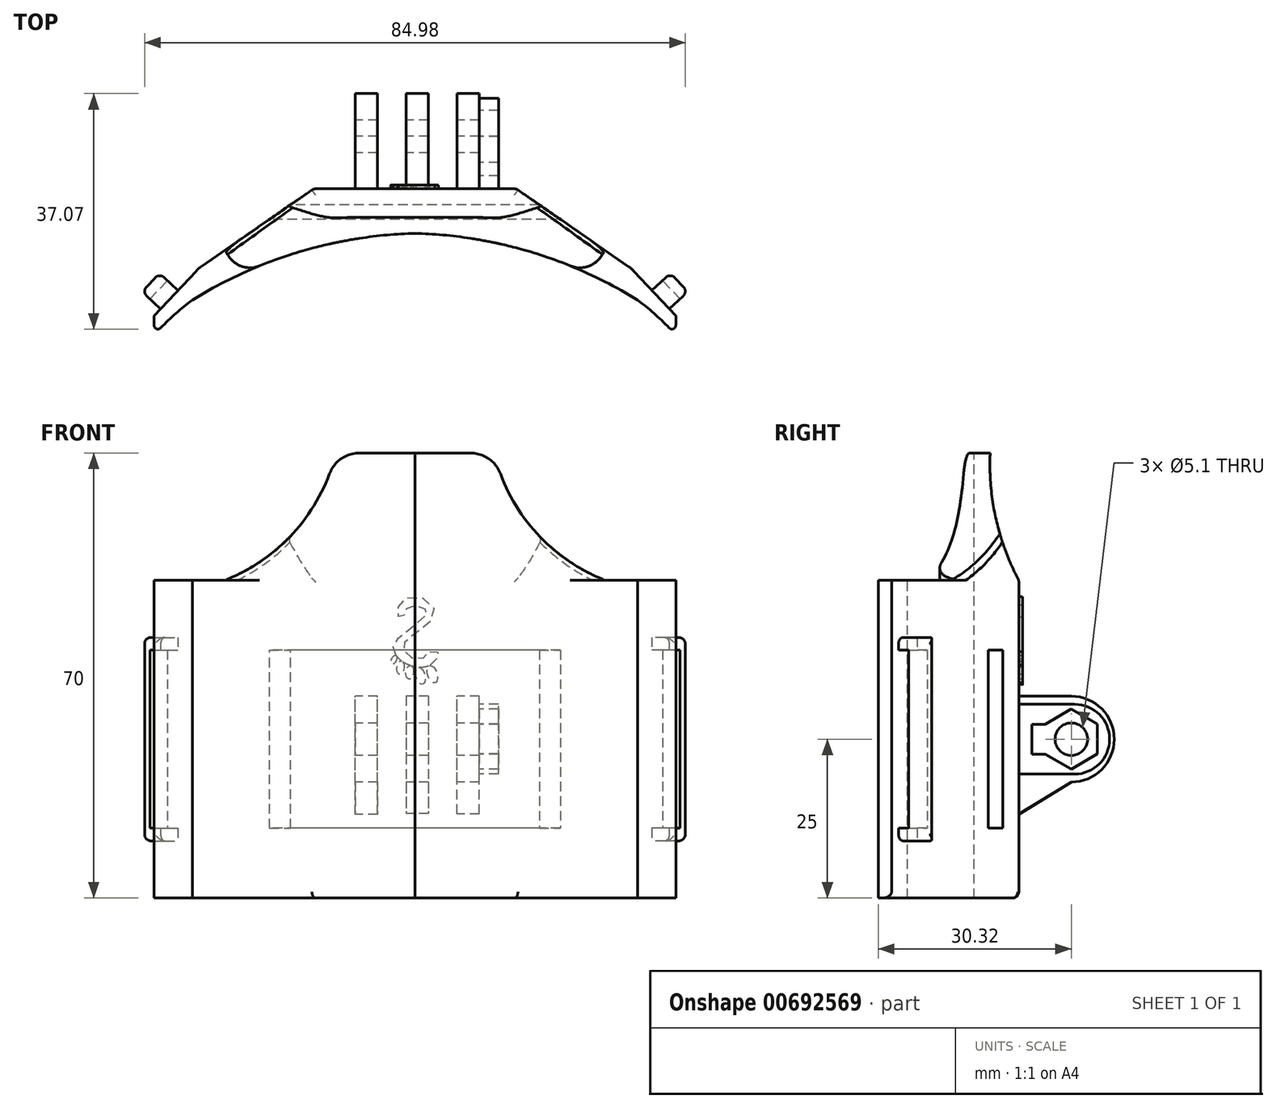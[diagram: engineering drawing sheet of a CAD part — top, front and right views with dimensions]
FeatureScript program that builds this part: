
annotation { "Feature Type Name" : "Feature", "Feature Type Description" : "" }
export const myFeature = defineFeature(function(context is Context, id is Id, definition is map)
    precondition{}
    {
        {
            var Q0;
            Q0=qCreatedBy(makeId("Top.planeOp"),FACE);
            var sketch = newSketch(context, id + "F0", { "sketchPlane" : qUnion([Q0])});
            skArc(sketch, "E0", {"start": v(0, 0) * mm, "mid": v(-18.2, -2.93) * mm, "end": v(-35, -10.5) * mm});
            skArc(sketch, "E1", {"start": v(-35, -10.5) * mm, "mid": v(-38.14, -13.1) * mm, "end": v(-41, -16) * mm});
            skLineSegment(sketch, "E2", {"start": v(-41, -16) * mm, "end": v(-41, -13) * mm});
            skLineSegment(sketch, "E3", {"start": v(0, 7) * mm, "end": v(-15.94, 7) * mm});
            skLineSegment(sketch, "E4", {"start": v(0, 0) * mm, "end": v(0, 7) * mm});
            skLineSegment(sketch, "E5", {"start": v(-41, -13) * mm, "end": v(-34, -5.5) * mm});
            skLineSegment(sketch, "E6", {"start": v(-34, -5.5) * mm, "end": v(-15.94, 7) * mm});
            skPoint(sketch, "E7", {"position": v(-41, -13) * mm});
            skSolve(sketch);
        }
        {
            var Q0;
            Q0=qSketchRegion(id+"F0",true);
            extrude(context, id + "F1", {"entities" : qUnion([Q0]), "oppositeDirection" : true, "depth" : 50 * mm, "offsetDistance" : 25 * mm});
        }
        {
            var Q0;
            Q0=qCreatedBy(makeId("Top.planeOp"),FACE);
            var sketch = newSketch(context, id + "F2", { "sketchPlane" : qUnion([Q0])});
            skLineSegment(sketch, "E8", {"start": v(0, 0) * mm, "end": v(0, 7) * mm});
            skLineSegment(sketch, "E9", {"start": v(0, 7) * mm, "end": v(-15.94, 7) * mm});
            skLineSegment(sketch, "E10", {"start": v(-15.94, 7) * mm, "end": v(-29.91, -2.68) * mm});
            skLineSegment(sketch, "E11", {"start": v(-29.91, -2.68) * mm, "end": v(-27.35, -6.38) * mm});
            skArc(sketch, "E12", {"start": v(0, 0) * mm, "mid": v(-14, -1.8) * mm, "end": v(-27.35, -6.38) * mm});
            skSolve(sketch);
        }
        {
            var Q0;
            Q0 = qSketchRegion(id + "F2", true);
            extrude(context, id + "F3", {"entities" : qUnion([Q0]), "operationType" : NewBodyOperationType.ADD, "depth" : 20 * mm, "offsetDistance" : 25 * mm});
        }
        {
            var Q0;
            Q0=makeQuery(id+"F3.boolean.opBoolean","MERGE",FACE,{"derivedFrom":[makeQuery(id+"F1.opExtrude","SWEPT_FACE",FACE,{"disambiguationData":[OSD([sQuery(id+"F0.wireOp",EDGE,"E3")])]}),makeQuery(id+"F3.opExtrude","SWEPT_FACE",FACE,{"disambiguationData":[OSD([sQuery(id+"F2.wireOp",EDGE,"E9")])]})]});
            var sketch = newSketch(context, id + "F4", { "sketchPlane" : qUnion([Q0])});
            skArc(sketch, "E13", {"start": v(12.03, 22.08) * mm, "mid": v(18.04, 8.66) * mm, "end": v(29.91, 0) * mm});
            skLineSegment(sketch, "E14", {"start": v(29.91, 0) * mm, "end": v(29.91, 20) * mm});
            skLineSegment(sketch, "E15", {"start": v(29.91, 20) * mm, "end": v(12.03, 22.08) * mm});
            skSolve(sketch);
        }
        {
            var Q0;
            Q0 = qSketchRegion(id + "F4", true);
            extrude(context, id + "F5", {"entities" : qUnion([Q0]), "operationType" : NewBodyOperationType.REMOVE, "oppositeDirection" : true, "depth" : 25 * mm, "offsetDistance" : 25 * mm});
        }
        {
            var Q0;
            Q0=qCreatedBy(makeId("Right.planeOp"),FACE);
            var sketch = newSketch(context, id + "F6", { "sketchPlane" : qUnion([Q0])});
            skLineSegment(sketch, "E16", {"start": v(7, 20) * mm, "end": v(7, 0) * mm});
            skArc(sketch, "E17", {"start": v(2.5, 20) * mm, "mid": v(3.4, 9.7) * mm, "end": v(7, 0) * mm});
            skLineSegment(sketch, "E18", {"start": v(7, 20) * mm, "end": v(2.5, 20) * mm});
            skSolve(sketch);
        }
        {
            var Q0;
            Q0 = qSketchRegion(id + "F6", true);
            extrude(context, id + "F7", {"entities" : qUnion([Q0]), "operationType" : NewBodyOperationType.REMOVE, "endBound" : BoundingType.UP_TO_NEXT, "oppositeDirection" : true, "depth" : 25 * mm, "offsetDistance" : 25 * mm});
        }
        {
            var Q0;
            Q0=makeQuery(id+"F1.opExtrude","SWEPT_FACE",FACE,{"disambiguationData":[OSD([sQuery(id+"F0.wireOp",EDGE,"E5")])]});
            var sketch = newSketch(context, id + "F8", { "sketchPlane" : qUnion([Q0])});
            skLineSegment(sketch, "E19.bottom", {"start": v(36, -9) * mm, "end": v(32, -9) * mm});
            skLineSegment(sketch, "E19.top", {"start": v(36, -41) * mm, "end": v(32, -41) * mm});
            skLineSegment(sketch, "E19.left", {"start": v(36, -9) * mm, "end": v(36, -41) * mm});
            skLineSegment(sketch, "E19.right", {"start": v(32, -9) * mm, "end": v(32, -41) * mm});
            skSolve(sketch);
        }
        {
            var Q0;
            Q0 = qSketchRegion(id + "F8", true);
            extrude(context, id + "F9", {"entities" : qUnion([Q0]), "operationType" : NewBodyOperationType.ADD, "depth" : 4 * mm, "offsetDistance" : 25 * mm});
        }
        {
            var Q0;
            Q0=makeQuery(id+"F1.opExtrude","SWEPT_FACE",FACE,{"disambiguationData":[OSD([sQuery(id+"F0.wireOp",EDGE,"E5")])]});
            var sketch = newSketch(context, id + "F10", { "sketchPlane" : qUnion([Q0])});
            skLineSegment(sketch, "E20.bottom", {"start": v(36, -39) * mm, "end": v(32, -39) * mm});
            skLineSegment(sketch, "E20.top", {"start": v(36, -11) * mm, "end": v(32, -11) * mm});
            skLineSegment(sketch, "E20.left", {"start": v(36, -39) * mm, "end": v(36, -11) * mm});
            skLineSegment(sketch, "E20.right", {"start": v(32, -39) * mm, "end": v(32, -11) * mm});
            skSolve(sketch);
        }
        {
            var Q0;
            Q0 = qSketchRegion(id + "F10", true);
            extrude(context, id + "F11", {"entities" : qUnion([Q0]), "operationType" : NewBodyOperationType.REMOVE, "depth" : 2.3 * mm, "offsetDistance" : 25 * mm});
        }
        {
            var Q0;
            Q0=qCreatedBy(makeId("Right.planeOp"),FACE);
            var sketch = newSketch(context, id + "F12", { "sketchPlane" : qUnion([Q0])});
            skLineSegment(sketch, "E21.bottom", {"start": v(4.5, -11) * mm, "end": v(2.2, -11) * mm});
            skLineSegment(sketch, "E21.top", {"start": v(4.5, -39) * mm, "end": v(2.2, -39) * mm});
            skLineSegment(sketch, "E21.left", {"start": v(4.5, -11) * mm, "end": v(4.5, -39) * mm});
            skLineSegment(sketch, "E21.right", {"start": v(2.2, -11) * mm, "end": v(2.2, -39) * mm});
            skSolve(sketch);
        }
        {
            var Q0;
            Q0=makeQuery(id+"F9.opExtrude","CAP_EDGE",EDGE,{"disambiguationData":[OSD([sQuery(id+"F8.wireOp",EDGE,"E19.left")])],"isStart":false});
            fillet(context, id + "F13", {"entities" : qUnion([Q0]), "radius" : 1 * mm, "tangentPropagation" : true, "allowEdgeOverflow" : false});
        }
        {
            var Q0;
            Q0=makeQuery(id+"F1.opExtrude","SWEPT_EDGE",EDGE,{"disambiguationData":[OSD([sQuery(id+"F0.wireOp",EDGE,"E1"),sQuery(id+"F0.wireOp",EDGE,"E2")])]});
            fillet(context, id + "F14", {"entities" : qUnion([Q0]), "radius" : 0.6 * mm, "tangentPropagation" : true, "allowEdgeOverflow" : false});
        }
        {
            var Q0;
            Q0=makeQuery(id+"F9.opExtrude","CAP_EDGE",EDGE,{"disambiguationData":[OSD([sQuery(id+"F8.wireOp",EDGE,"E19.right")])],"isStart":false});
            var Q1;
            Q1=makeQuery(id+"F9.opExtrude","CAP_EDGE",EDGE,{"disambiguationData":[OSD([sQuery(id+"F8.wireOp",EDGE,"E19.bottom")])],"isStart":false});
            var Q2;
            Q2=makeQuery(id+"F9.opExtrude","CAP_EDGE",EDGE,{"disambiguationData":[OSD([sQuery(id+"F8.wireOp",EDGE,"E19.top")])],"isStart":false});
            fillet(context, id + "F15", {"entities" : qUnion([Q0, Q1, Q2]), "radius" : 1 * mm, "tangentPropagation" : true, "allowEdgeOverflow" : false});
        }
        {
            var Q0;
            Q0=makeQuery(id+"F1.opExtrude","SWEPT_EDGE",EDGE,{"disambiguationData":[OSD([sQuery(id+"F0.wireOp",EDGE,"E5"),sQuery(id+"F0.wireOp",EDGE,"E6")])]});
            fillet(context, id + "F16", {"entities" : qUnion([Q0]), "radius" : 5 * mm, "tangentPropagation" : true, "allowEdgeOverflow" : false});
        }
        {
            var Q0;
            Q0=makeQuery(id+"F3.opExtrude","SWEPT_EDGE",EDGE,{"disambiguationData":[OSD([sQuery(id+"F2.wireOp",EDGE,"E11"),sQuery(id+"F2.wireOp",EDGE,"E12")])]});
            fillet(context, id + "F17", {"entities" : qUnion([Q0]), "radius" : 4 * mm, "tangentPropagation" : true, "allowEdgeOverflow" : false});
        }
        {
            var Q0;
            Q0=makeQuery(id+"F1.opExtrude","CAP_EDGE",EDGE,{"disambiguationData":[OSD([sQuery(id+"F0.wireOp",EDGE,"E5")])],"isStart":false});
            fillet(context, id + "F18", {"entities" : qUnion([Q0]), "radius" : 1 * mm, "tangentPropagation" : true, "allowEdgeOverflow" : false});
        }
        {
            var Q0;
            Q0=makeQuery(id+"F1.opExtrude","SWEPT_BODY",BODY,{"disambiguationData":[OSD([sQuery(id+"F0.wireOp",EDGE,"E0"),sQuery(id+"F0.wireOp",EDGE,"E1"),sQuery(id+"F0.wireOp",EDGE,"E2"),sQuery(id+"F0.wireOp",EDGE,"E3"),sQuery(id+"F0.wireOp",EDGE,"E4"),sQuery(id+"F0.wireOp",EDGE,"E5"),sQuery(id+"F0.wireOp",EDGE,"E6")])]});
            var Q1;
            Q1=qCreatedBy(makeId("Right.planeOp"),FACE);
            mirror(context, id + "F19", {"operationType" : NewBodyOperationType.ADD, "entities" : qUnion([Q0]), "mirrorPlane" : qUnion([Q1])});
        }
        {
            var Q0;
            {var subQ0=makeQuery(id+"F1.opExtrude","SWEPT_FACE",FACE,{"disambiguationData":[OSD([sQuery(id+"F0.wireOp",EDGE,"E3")])]});Q0=makeQuery(id+"F19.boolean.opBoolean","MERGE",FACE,{"derivedFrom":[subQ0,makeQuery(id+"F19.opPattern","COPY",FACE,{"derivedFrom":subQ0,"instanceName":"1"})]});}
            fillet(context, id + "F20", {"entities" : qUnion([Q0]), "radius" : 1 * mm, "tangentPropagation" : true, "allowEdgeOverflow" : false});
        }
        {
            var Q0;
            Q0 = qSketchRegion(id + "F12", true);
            extrude(context, id + "F21", {"entities" : qUnion([Q0]), "operationType" : NewBodyOperationType.REMOVE, "depth" : 25 * mm, "offsetDistance" : 25 * mm, "hasSecondDirection" : true, "secondDirectionOppositeDirection" : true, "secondDirectionDepth" : 25 * mm});
        }
        {
            var Q0;
            {var subQ0=makeQuery(id+"F7.boolean.opBoolean","COPY",EDGE,{"derivedFrom":makeQuery(id+"F7.opExtrude","SWEPT_EDGE",EDGE,{"disambiguationData":[OSD([sQuery(id+"F6.wireOp",EDGE,"E17"),sQuery(id+"F6.wireOp",EDGE,"E18")])]})});Q0=makeQuery(id+"F19.boolean.opBoolean","MERGE",EDGE,{"derivedFrom":[subQ0,makeQuery(id+"F19.opPattern","COPY",EDGE,{"derivedFrom":subQ0,"instanceName":"1"})]});}
            var Q1;
            Q1=makeQuery(id+"F7.boolean.opBoolean","COPY",EDGE,{"derivedFrom":makeQuery(id+"F7.opExtrude","TWEAK_EDGE",EDGE,{"derivedFrom":[makeQuery(id+"F5.boolean.opBoolean","COPY",FACE,{"derivedFrom":makeQuery(id+"F5.opExtrude","SWEPT_FACE",FACE,{"disambiguationData":[OSD([sQuery(id+"F4.wireOp",EDGE,"E13")])]})}),makeQuery(id+"F6.imprint","IMPRINT",EDGE,{"derivedFrom":sQuery(id+"F6.wireOp",EDGE,"E17")})]})});
            var Q2;
            Q2=makeQuery(id+"F19.opPattern","COPY",EDGE,{"derivedFrom":makeQuery(id+"F7.boolean.opBoolean","COPY",EDGE,{"derivedFrom":makeQuery(id+"F7.opExtrude","TWEAK_EDGE",EDGE,{"derivedFrom":[makeQuery(id+"F5.boolean.opBoolean","COPY",FACE,{"derivedFrom":makeQuery(id+"F5.opExtrude","SWEPT_FACE",FACE,{"disambiguationData":[OSD([sQuery(id+"F4.wireOp",EDGE,"E13")])]})}),makeQuery(id+"F6.imprint","IMPRINT",EDGE,{"derivedFrom":sQuery(id+"F6.wireOp",EDGE,"E17")})]})}),"instanceName":"1"});
            var Q3;
            Q3=makeQuery(id+"F5.boolean.opBoolean","INTERSECT",EDGE,{"derivedFrom":[makeQuery(id+"F3.boolean.opBoolean","MERGE",FACE,{"derivedFrom":[makeQuery(id+"F1.opExtrude","SWEPT_FACE",FACE,{"disambiguationData":[OSD([sQuery(id+"F0.wireOp",EDGE,"E6")])]}),makeQuery(id+"F3.opExtrude","SWEPT_FACE",FACE,{"disambiguationData":[OSD([sQuery(id+"F2.wireOp",EDGE,"E10")])]})]}),makeQuery(id+"F5.opExtrude","SWEPT_FACE",FACE,{"disambiguationData":[OSD([sQuery(id+"F4.wireOp",EDGE,"E13")])]})]});
            var Q4;
            Q4=makeQuery(id+"F7.boolean.opBoolean","COPY",EDGE,{"derivedFrom":makeQuery(id+"F7.opExtrude","TWEAK_EDGE",EDGE,{"derivedFrom":[makeQuery(id+"F3.boolean.opBoolean","MERGE",FACE,{"derivedFrom":[makeQuery(id+"F1.opExtrude","SWEPT_FACE",FACE,{"disambiguationData":[OSD([sQuery(id+"F0.wireOp",EDGE,"E6")])]}),makeQuery(id+"F3.opExtrude","SWEPT_FACE",FACE,{"disambiguationData":[OSD([sQuery(id+"F2.wireOp",EDGE,"E10")])]})]}),makeQuery(id+"F6.imprint","IMPRINT",EDGE,{"derivedFrom":sQuery(id+"F6.wireOp",EDGE,"E17")})]})});
            var Q5;
            Q5=makeQuery(id+"F19.opPattern","COPY",EDGE,{"derivedFrom":makeQuery(id+"F7.boolean.opBoolean","COPY",EDGE,{"derivedFrom":makeQuery(id+"F7.opExtrude","TWEAK_EDGE",EDGE,{"derivedFrom":[makeQuery(id+"F3.boolean.opBoolean","MERGE",FACE,{"derivedFrom":[makeQuery(id+"F1.opExtrude","SWEPT_FACE",FACE,{"disambiguationData":[OSD([sQuery(id+"F0.wireOp",EDGE,"E6")])]}),makeQuery(id+"F3.opExtrude","SWEPT_FACE",FACE,{"disambiguationData":[OSD([sQuery(id+"F2.wireOp",EDGE,"E10")])]})]}),makeQuery(id+"F6.imprint","IMPRINT",EDGE,{"derivedFrom":sQuery(id+"F6.wireOp",EDGE,"E17")})]})}),"instanceName":"1"});
            var Q6;
            Q6=makeQuery(id+"F19.opPattern","COPY",EDGE,{"derivedFrom":makeQuery(id+"F5.boolean.opBoolean","INTERSECT",EDGE,{"derivedFrom":[makeQuery(id+"F3.boolean.opBoolean","MERGE",FACE,{"derivedFrom":[makeQuery(id+"F1.opExtrude","SWEPT_FACE",FACE,{"disambiguationData":[OSD([sQuery(id+"F0.wireOp",EDGE,"E6")])]}),makeQuery(id+"F3.opExtrude","SWEPT_FACE",FACE,{"disambiguationData":[OSD([sQuery(id+"F2.wireOp",EDGE,"E10")])]})]}),makeQuery(id+"F5.opExtrude","SWEPT_FACE",FACE,{"disambiguationData":[OSD([sQuery(id+"F4.wireOp",EDGE,"E13")])]})]}),"instanceName":"1"});
            fillet(context, id + "F22", {"entities" : qUnion([Q0, Q1, Q2, Q3, Q4, Q5, Q6]), "radius" : 1 * mm, "tangentPropagation" : true, "allowEdgeOverflow" : false});
        }
        {
            var Q0;
            {var subQ0=makeQuery(id+"F3.boolean.opBoolean","MERGE",FACE,{"derivedFrom":[makeQuery(id+"F1.opExtrude","SWEPT_FACE",FACE,{"disambiguationData":[OSD([sQuery(id+"F0.wireOp",EDGE,"E3")])]}),makeQuery(id+"F3.opExtrude","SWEPT_FACE",FACE,{"disambiguationData":[OSD([sQuery(id+"F2.wireOp",EDGE,"E9")])]})]});Q0=makeQuery(id+"F19.boolean.opBoolean","MERGE",FACE,{"derivedFrom":[subQ0,makeQuery(id+"F19.opPattern","COPY",FACE,{"derivedFrom":subQ0,"instanceName":"1"})]});}
            var sketch = newSketch(context, id + "F23", { "sketchPlane" : qUnion([Q0])});
            skLineSegment(sketch, "E22.bottom", {"start": v(-10.12, -31.75) * mm, "end": v(-6.62, -31.75) * mm});
            skLineSegment(sketch, "E22.top", {"start": v(-10.12, -18.25) * mm, "end": v(-6.62, -18.25) * mm});
            skLineSegment(sketch, "E22.left", {"start": v(-10.12, -31.75) * mm, "end": v(-10.12, -18.25) * mm});
            skLineSegment(sketch, "E22.right", {"start": v(-6.62, -31.75) * mm, "end": v(-6.62, -18.25) * mm});
            skLineSegment(sketch, "E23.bottom", {"start": v(-2.12, -18.25) * mm, "end": v(1.38, -18.25) * mm});
            skLineSegment(sketch, "E23.top", {"start": v(-2.12, -31.75) * mm, "end": v(1.38, -31.75) * mm});
            skLineSegment(sketch, "E23.left", {"start": v(-2.12, -18.25) * mm, "end": v(-2.12, -31.75) * mm});
            skLineSegment(sketch, "E23.right", {"start": v(1.38, -18.25) * mm, "end": v(1.38, -31.75) * mm});
            skLineSegment(sketch, "E24.bottom", {"start": v(5.88, -31.75) * mm, "end": v(9.38, -31.75) * mm});
            skLineSegment(sketch, "E24.top", {"start": v(5.88, -18.25) * mm, "end": v(9.38, -18.25) * mm});
            skLineSegment(sketch, "E24.left", {"start": v(5.88, -31.75) * mm, "end": v(5.88, -18.25) * mm});
            skLineSegment(sketch, "E24.right", {"start": v(9.38, -31.75) * mm, "end": v(9.38, -18.25) * mm});
            skSolve(sketch);
        }
        {
            var Q0;
            Q0 = qSketchRegion(id + "F23", true);
            extrude(context, id + "F24", {"entities" : qUnion([Q0]), "operationType" : NewBodyOperationType.ADD, "depth" : 15 * mm, "offsetDistance" : 25 * mm});
        }
        {
            var Q0;
            Q0=makeQuery(id+"F24.opExtrude","CAP_EDGE",EDGE,{"disambiguationData":[OSD([sQuery(id+"F23.wireOp",EDGE,"E24.bottom")])],"isStart":false});
            var Q1;
            Q1=makeQuery(id+"F24.opExtrude","CAP_EDGE",EDGE,{"disambiguationData":[OSD([sQuery(id+"F23.wireOp",EDGE,"E23.top")])],"isStart":false});
            var Q2;
            Q2=makeQuery(id+"F24.opExtrude","CAP_EDGE",EDGE,{"disambiguationData":[OSD([sQuery(id+"F23.wireOp",EDGE,"E22.bottom")])],"isStart":false});
            var Q3;
            Q3=makeQuery(id+"F24.opExtrude","CAP_EDGE",EDGE,{"disambiguationData":[OSD([sQuery(id+"F23.wireOp",EDGE,"E24.top")])],"isStart":false});
            var Q4;
            Q4=makeQuery(id+"F24.opExtrude","CAP_EDGE",EDGE,{"disambiguationData":[OSD([sQuery(id+"F23.wireOp",EDGE,"E23.bottom")])],"isStart":false});
            var Q5;
            Q5=makeQuery(id+"F24.opExtrude","CAP_EDGE",EDGE,{"disambiguationData":[OSD([sQuery(id+"F23.wireOp",EDGE,"E22.top")])],"isStart":false});
            fillet(context, id + "F25", {"entities" : qUnion([Q0, Q1, Q2, Q3, Q4, Q5]), "radius" : 6.75 * mm, "tangentPropagation" : true, "allowEdgeOverflow" : false});
        }
        {
            var Q0;
            Q0=makeQuery(id+"F24.opExtrude","SWEPT_FACE",FACE,{"disambiguationData":[OSD([sQuery(id+"F23.wireOp",EDGE,"E24.right")])]});
            var sketch = newSketch(context, id + "F26", { "sketchPlane" : qUnion([Q0])});
            skCircle(sketch, "E25", {"center": v(-15.25, -25) * mm, "radius": 2.55 * mm});
            skSolve(sketch);
        }
        {
            var Q0;
            Q0 = qSketchRegion(id + "F26", true);
            extrude(context, id + "F27", {"entities" : qUnion([Q0]), "operationType" : NewBodyOperationType.REMOVE, "endBound" : BoundingType.THROUGH_ALL, "oppositeDirection" : true, "depth" : 25 * mm, "offsetDistance" : 25 * mm});
        }
        {
            var Q0;
            Q0=makeQuery(id+"F24.opExtrude","SWEPT_FACE",FACE,{"disambiguationData":[OSD([sQuery(id+"F23.wireOp",EDGE,"E24.right")])]});
            var sketch = newSketch(context, id + "F28", { "sketchPlane" : qUnion([Q0])});
            skLineSegment(sketch, "E26", {"start": v(-7, -31.75) * mm, "end": v(-15.25, -31.75) * mm});
            skLineSegment(sketch, "E27", {"start": v(-15.25, -31.75) * mm, "end": v(-7, -36.82) * mm});
            skLineSegment(sketch, "E28", {"start": v(-7, -36.82) * mm, "end": v(-7, -31.75) * mm});
            skSolve(sketch);
        }
        {
            var Q0;
            Q0 = qSketchRegion(id + "F28", true);
            extrude(context, id + "F29", {"entities" : qUnion([Q0]), "operationType" : NewBodyOperationType.ADD, "oppositeDirection" : true, "depth" : 3.5 * mm, "offsetDistance" : 25 * mm});
        }
        {
            var Q0;
            Q0=makeQuery(id+"F24.opExtrude","SWEPT_FACE",FACE,{"disambiguationData":[OSD([sQuery(id+"F23.wireOp",EDGE,"E23.right")])]});
            var sketch = newSketch(context, id + "F30", { "sketchPlane" : qUnion([Q0])});
            skLineSegment(sketch, "E29", {"start": v(-7, -31.75) * mm, "end": v(-15.25, -31.75) * mm});
            skLineSegment(sketch, "E30", {"start": v(-15.25, -31.75) * mm, "end": v(-6.96, -36.75) * mm});
            skLineSegment(sketch, "E31", {"start": v(-6.96, -36.75) * mm, "end": v(-7, -31.75) * mm});
            skSolve(sketch);
        }
        {
            var Q0;
            Q0 = qSketchRegion(id + "F30", true);
            extrude(context, id + "F31", {"entities" : qUnion([Q0]), "operationType" : NewBodyOperationType.ADD, "oppositeDirection" : true, "depth" : 3.5 * mm, "offsetDistance" : 25 * mm});
        }
        {
            var Q0;
            Q0=makeQuery(id+"F24.opExtrude","SWEPT_FACE",FACE,{"disambiguationData":[OSD([sQuery(id+"F23.wireOp",EDGE,"E22.right")])]});
            var sketch = newSketch(context, id + "F32", { "sketchPlane" : qUnion([Q0])});
            skLineSegment(sketch, "E32", {"start": v(-15.25, -31.75) * mm, "end": v(-7, -31.75) * mm});
            skLineSegment(sketch, "E33", {"start": v(-7, -31.75) * mm, "end": v(-7, -36.75) * mm});
            skLineSegment(sketch, "E34", {"start": v(-7, -36.75) * mm, "end": v(-15.25, -31.75) * mm});
            skSolve(sketch);
        }
        {
            var Q0;
            Q0 = qSketchRegion(id + "F32", true);
            extrude(context, id + "F33", {"entities" : qUnion([Q0]), "operationType" : NewBodyOperationType.ADD, "oppositeDirection" : true, "depth" : 3.5 * mm, "offsetDistance" : 25 * mm});
        }
        {
            var Q0;
            Q0=makeQuery(id+"F5.boolean.opBoolean","INTERSECT",EDGE,{"derivedFrom":[makeQuery(id+"F3.opExtrude","CAP_FACE",FACE,{"disambiguationData":[OSD([sQuery(id+"F2.wireOp",EDGE,"E8"),sQuery(id+"F2.wireOp",EDGE,"E9"),sQuery(id+"F2.wireOp",EDGE,"E10"),sQuery(id+"F2.wireOp",EDGE,"E11"),sQuery(id+"F2.wireOp",EDGE,"E12")])],"isStart":false}),makeQuery(id+"F5.opExtrude","SWEPT_FACE",FACE,{"disambiguationData":[OSD([sQuery(id+"F4.wireOp",EDGE,"E13")])]})]});
            fillet(context, id + "F34", {"entities" : qUnion([Q0]), "radius" : 5 * mm, "tangentPropagation" : true, "allowEdgeOverflow" : false});
        }
        {
            var Q0;
            Q0=makeQuery(id+"F19.opPattern","COPY",EDGE,{"derivedFrom":makeQuery(id+"F5.boolean.opBoolean","INTERSECT",EDGE,{"derivedFrom":[makeQuery(id+"F3.opExtrude","CAP_FACE",FACE,{"disambiguationData":[OSD([sQuery(id+"F2.wireOp",EDGE,"E8"),sQuery(id+"F2.wireOp",EDGE,"E9"),sQuery(id+"F2.wireOp",EDGE,"E10"),sQuery(id+"F2.wireOp",EDGE,"E11"),sQuery(id+"F2.wireOp",EDGE,"E12")])],"isStart":false}),makeQuery(id+"F5.opExtrude","SWEPT_FACE",FACE,{"disambiguationData":[OSD([sQuery(id+"F4.wireOp",EDGE,"E13")])]})]}),"instanceName":"1"});
            fillet(context, id + "F35", {"entities" : qUnion([Q0]), "radius" : 5 * mm, "tangentPropagation" : true, "allowEdgeOverflow" : false});
        }
        {
            var Q0;
            {var subQ0=makeQuery(id+"F3.boolean.opBoolean","MERGE",FACE,{"derivedFrom":[makeQuery(id+"F1.opExtrude","SWEPT_FACE",FACE,{"disambiguationData":[OSD([sQuery(id+"F0.wireOp",EDGE,"E3")])]}),makeQuery(id+"F3.opExtrude","SWEPT_FACE",FACE,{"disambiguationData":[OSD([sQuery(id+"F2.wireOp",EDGE,"E9")])]})]});Q0=makeQuery(id+"F19.boolean.opBoolean","MERGE",FACE,{"derivedFrom":[subQ0,makeQuery(id+"F19.opPattern","COPY",FACE,{"derivedFrom":subQ0,"instanceName":"1"})]});}
            var sketch = newSketch(context, id + "F36", { "sketchPlane" : qUnion([Q0])});
            skEllipse(sketch, "E35", {"center": v(3.3, -12.5) * mm, "majorRadius": 0.75 * mm, "minorRadius": 0.38 * mm, "majorAxis": v(-0.42, 0.9)});
            skEllipse(sketch, "E36", {"center": v(2.26, -13.77) * mm, "majorRadius": 1.06 * mm, "minorRadius": 0.56 * mm, "majorAxis": v(-0.1, 1)});
            skEllipse(sketch, "E37", {"center": v(0.83, -14.5) * mm, "majorRadius": 1.08 * mm, "minorRadius": 0.6 * mm, "majorAxis": v(-0.1, 1)});
            skEllipse(sketch, "E38", {"center": v(-0.88, -15.06) * mm, "majorRadius": 1.36 * mm, "minorRadius": 0.7 * mm, "majorAxis": v(0.23, 0.97)});
            skEllipse(sketch, "E39", {"center": v(-2.72, -14.77) * mm, "majorRadius": 1.42 * mm, "minorRadius": 0.73 * mm, "majorAxis": v(0.3, 0.95)});
            skPoint(sketch, "E40.23.internal.snap0", {"position": v(0.72, -13.42) * mm});
            skPoint(sketch, "E40.40.internal.snap0", {"position": v(-0.56, -13.74) * mm});
            skPoint(sketch, "E40.47.internal.snap0", {"position": v(-0.56, -13.74) * mm});
            skPoint(sketch, "E40.51.internal.snap0", {"position": v(-2.29, -13.42) * mm});
            skFitSpline(sketch, "E40", {"points": [v(-3.61, -11.3) * mm, v(-3.71, -11.47) * mm, v(-3.68, -11.73) * mm, v(-3.47, -12.27) * mm, v(-3.06, -12.82) * mm, v(-2.49, -13.3) * mm, v(-1.53, -13.67) * mm, v(-0.22, -13.67) * mm, v(1.08, -13.28) * mm, v(2.08, -12.73) * mm, v(2.96, -11.84) * mm, v(3.35, -11.35) * mm, v(3.43, -10.68) * mm, v(3.25, -9.84) * mm, v(2.77, -9.24) * mm, v(1.3, -7.99) * mm, v(-1.3, -5.95) * mm, v(-1.82, -5.38) * mm, v(-1.9, -5.1) * mm, v(-1.84, -4.83) * mm, v(-1.66, -4.6) * mm, v(-1.22, -4.25) * mm, v(-0.36, -4) * mm, v(0.72, -4) * mm, v(1.31, -4.4) * mm, v(1.38, -4.89) * mm, v(1.38, -5.3) * mm, v(1.69, -5.54) * mm, v(1.9, -5.67) * mm, v(2.27, -5.83) * mm, v(2.47, -5.8) * mm, v(2.63, -5.55) * mm, v(2.6, -4.6) * mm, v(2.56, -4.05) * mm, v(1.92, -3.1) * mm, v(0.42, -2.6) * mm, v(-1.43, -2.9) * mm, v(-2.8, -4.07) * mm, v(-3.09, -5.52) * mm, v(-2.06, -6.82) * mm, v(-0.56, -7.97) * mm, v(1.38, -9.5) * mm, v(1.79, -10.04) * mm, v(1.82, -10.46) * mm, v(1.72, -11.15) * mm, v(1.19, -11.7) * mm, v(0.38, -12.2) * mm, v(-0.56, -12.38) * mm, v(-1.45, -12.17) * mm, v(-1.98, -11.52) * mm, v(-2.1, -11.3) * mm, v(-2.29, -11.23) * mm, v(-2.8, -11.22) * mm, v(-3.61, -11.3) * mm]});
            skSolve(sketch);
        }
        {
            var Q0;
            Q0 = qSketchRegion(id + "F36", true);
            extrude(context, id + "F37", {"entities" : qUnion([Q0]), "operationType" : NewBodyOperationType.ADD, "depth" : 0.6 * mm, "offsetDistance" : 25 * mm});
        }
        {
            var Q0;
            Q0=makeQuery(id+"F33.boolean.opBoolean","MERGE",FACE,{"derivedFrom":[makeQuery(id+"F24.opExtrude","SWEPT_FACE",FACE,{"disambiguationData":[OSD([sQuery(id+"F23.wireOp",EDGE,"E22.left")])]}),makeQuery(id+"F33.opExtrude","CAP_FACE",FACE,{"disambiguationData":[OSD([sQuery(id+"F32.wireOp",EDGE,"E32"),sQuery(id+"F32.wireOp",EDGE,"E33"),sQuery(id+"F32.wireOp",EDGE,"E34")])],"isStart":false})]});
            var sketch = newSketch(context, id + "F38", { "sketchPlane" : qUnion([Q0])});
            skLineSegment(sketch, "E41", {"start": v(7, -19.5) * mm, "end": v(21.27, -19.5) * mm});
            skLineSegment(sketch, "E42", {"start": v(21.27, -19.5) * mm, "end": v(21.27, -30.5) * mm});
            skLineSegment(sketch, "E43", {"start": v(21.27, -30.5) * mm, "end": v(7, -30.5) * mm});
            skLineSegment(sketch, "E44", {"start": v(7, -30.5) * mm, "end": v(7, -19.5) * mm});
            skCircle(sketch, "E45.cCircle", {"center": v(15.25, -25) * mm, "radius": 4.1 * mm, "construction": true});
            skLineSegment(sketch, "E45.0", {"start": v(15.21, -20.27) * mm, "end": v(19.32, -22.6) * mm});
            skLineSegment(sketch, "E45.1", {"start": v(19.32, -22.6) * mm, "end": v(19.36, -27.33) * mm});
            skLineSegment(sketch, "E45.2", {"start": v(19.36, -27.33) * mm, "end": v(15.29, -29.73) * mm});
            skLineSegment(sketch, "E45.3", {"start": v(15.29, -29.73) * mm, "end": v(11.18, -27.4) * mm});
            skLineSegment(sketch, "E45.5", {"start": v(11.14, -22.67) * mm, "end": v(15.21, -20.27) * mm});
            skPoint(sketch, "E45.0.midPoint", {"position": v(17.27, -21.44) * mm});
            skLineSegment(sketch, "E46", {"start": v(11.14, -22.67) * mm, "end": v(9.03, -22.67) * mm});
            skLineSegment(sketch, "E47", {"start": v(9.03, -22.67) * mm, "end": v(9.03, -27.4) * mm});
            skLineSegment(sketch, "E48", {"start": v(9.03, -27.4) * mm, "end": v(11.18, -27.4) * mm});
            skSolve(sketch);
        }
        {
            var Q0;
            Q0 = qSketchRegion(id + "F38", true);
            extrude(context, id + "F39", {"entities" : qUnion([Q0]), "operationType" : NewBodyOperationType.ADD, "depth" : 3 * mm, "offsetDistance" : 25 * mm});
        }
        {
            var Q0;
            Q0=makeQuery(id+"F39.opExtrude","SWEPT_EDGE",EDGE,{"disambiguationData":[OSD([sQuery(id+"F38.wireOp",EDGE,"E42"),sQuery(id+"F38.wireOp",EDGE,"E43")])]});
            var Q1;
            Q1=makeQuery(id+"F39.opExtrude","SWEPT_EDGE",EDGE,{"disambiguationData":[OSD([sQuery(id+"F38.wireOp",EDGE,"E41"),sQuery(id+"F38.wireOp",EDGE,"E42")])]});
            fillet(context, id + "F40", {"entities" : qUnion([Q0, Q1]), "radius" : 5.5 * mm, "tangentPropagation" : true, "allowEdgeOverflow" : false});
        }
    });
